# Revit family: SVT2
name_source: partatom
category: Mechanical Equipment
revit_build: Autodesk Revit 2015 (Build: 20140606_1530(x64)
units: mm (PartAtom-declared; Revit-internal decimal feet)

## types (2) — shared parameters
Apparent Load = 1080 VA
Catalogue Pages = http://www.nuaire.info
Classification.Uniclass.Pr.Description = Axial flow fans
Classification.Uniclass.Pr.Number = Pr_65_67_29_05
Description = Car Park Impulse Fan
Electrical Phase = 3
Fax Number = +44(0)2920-858-222
Full Load Current = 3 A
I&M Manual = http://www.nuaire.info
IFCExportAs = IfcFanType
Length = 2303 mm
Manufacturer = Nuaire
Manufacturer Name = Nuaire
Nominal Motor Rating = 1100 W
Nominal Motor Speed (rpm) = 2775
Number of Connection Poles = 3
Number of Motor Poles = 4
OmniClass Number = 23-33 31 19 11
OmniClass Title = Axial Fans
Postcode = CF83 1NA
Revit Family Last Revised = 30/10/18
Starting Current = 15 A
Telephone Number = +44(0)2920-858-200
URL = http://www.nuaire.co.uk
Unit Description = Car Park Impulse Fan
VAT Registration Number = 877308
Voltage = 400 V
Warranty Period = 3 Years
Weatherproof or Internal Only = Internal
Width = 702 mm

## per-type parameters (varying)
| type | 1E | 2E | Height | Hole Centre | Hole Diameter | Weight |
| SVT2-1E | Yes | No | 329 mm  [stored 1.0794 ft] | 163 mm | 315 mm  [stored 1.03346 ft] | 94.00 kg |
| SVT2-2E | No | Yes | 404 mm  [stored 1.32546 ft] | 200 mm | 355 mm | 113.00 kg |

note: column(s) folded — value = type name in every type: Model, Nuaire Model Code

note: [stored X ft] marks values corroborated as IEEE doubles in the binary element streams (Revit-internal decimal feet)

## geometry (parser evidence)
native form markers: Blend x20, Sweep x6
no freeform markers — native parametric forms only
